# Revit family: Basin_Catch_12X24-Zurn-Z887-12
name_source: partatom
category: Plumbing Fixtures
units: mm (PartAtom-declared; Revit-internal decimal feet)

## family parameters
Always vertical = Yes
Cut with Voids When Loaded = No
Maintain Annotation Orientation = No
OmniClass Number = 23.70.50.21.24.14
OmniClass Title = Deck Waste Water Drains
Part Type = Normal
Room Calculation Point = No
Round Connector Dimension = Use Radius
Shared = No
Work Plane-Based = No

## types (6) — shared parameters
Assembly Code = D2030300
CW Connection = No
Default Elevation = 20 "
Description = 12 [305] WIDE REVEAL BY 24-9/16 [624] LONG CATCH BASIN
Grate = Ductile Iron - Zurn - Polished
HW Connection = No
Main Material = Polymer - Zurn - HDPE - Grey
Manufacturer = Zurn Water, LLC
Manufacurer Brand = Zurn
Model = Z887-12
Modified Date = 12/02/2025
Product Documentation Link = https://files.zurn.com
Product Page URL = https://www.zurn.com
Product data url = https://www.bimobject.com
URL = www.zurn.com
Vent Connection = No
WFU = 1
Waste Connection = Yes
zero-valued in all types: CWFU, HWFU

## per-type parameters (varying)
| type | Bottom Outlet | End Outlet | Pipe Size_A Bottom Inside Diameter | Pipe Size_A Bottom Inside Radius | Pipe Size_A Bottom Nominal Diameter | Pipe Size_A Bottom Nominal Radius | Pipe Size_A Bottom Outer Diameter | Pipe Size_A Bottom Outer Radius | Pipe Size_A End Inside Diameter | Pipe Size_A End Inside Radius | Pipe Size_A End Nominal Diameter | Pipe Size_A End Nominal Radius | Pipe Size_A End Outer Diameter | Pipe Size_A End Outer Radius | Type Comments |
| Z887-12 With 3 Inch No Hub End Outlet | No | Yes | 3.068 " | 1.534 " | 3 " | 1.5 " | 3.5 " | 1.75 " | 3.068 " | 1.534 " | 3 " | 1.5 " | 3.5 " | 1.75 " | Z887-12 With 3 Inch No Hub End Outlet |
| Z887-12 With 4 Inch No Hub End Outlet | No | Yes | 4.026 " | 2.013 " | 4 " | 2 " | 4.5 " | 2.25 " | 4.026 " | 2.013 " | 4 " | 2 " | 4.5 " | 2.25 " | Z887-12  With 4 Inch No Hub End Outlet |
| Z887-12 With 6 Inch No Hub End Outlet | No | Yes | 6.065 " | 3.033 " | 6 " | 3 " | 6.625 " | 3.313 " | 6.065 " | 3.033 " | 6 " | 3 " | 6.625 " | 3.313 " | Z887-12 With 6 Inch No Hub End Outlet |
| Z887-12 With 6 Inch No Hub Bottom Outlet | Yes | No | 6.065 " | 3.033 " | 6 " | 3 " | 6.625 " | 3.313 " | 6.065 " | 3.033 " | 6 " | 3 " | 6.625 " | 3.313 " | Z887-12 With 6 Inch No Hub Bottom Outlet |
| Z887-12 With 4 Inch No Hub Bottom Outlet | Yes | No | 4.026 " | 2.013 " | 4 " | 2 " | 4.5 " | 2.25 " | 4.026 " | 2.013 " | 4 " | 2 " | 4.5 " | 2.25 " | Z887-12 With 4 Inch No Hub Bottom Outlet |
| Z887-12 With 3 Inch No Hub Bottom Outlet | Yes | No | 3.068 " | 1.534 " | 3 " | 1.5 " | 3.5 " | 1.75 " | 3.068 " | 1.534 " | 3 " | 1.5 " | 3.5 " | 1.75 " | Z887-12 With 3 Inch No Hub Bottom Outlet |

## geometry (parser evidence)
native form markers: Blend x6, Sweep x3
no freeform markers — native parametric forms only
